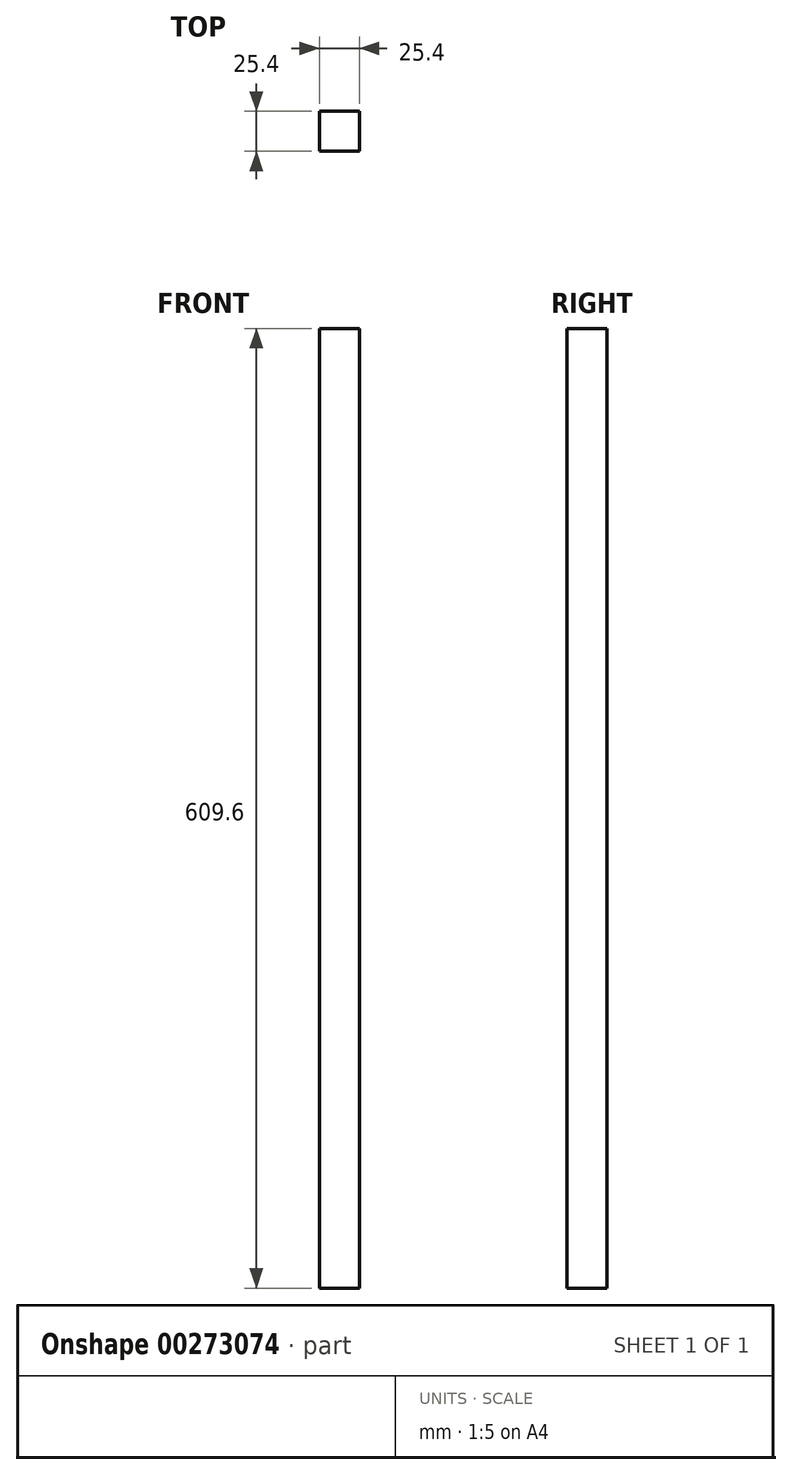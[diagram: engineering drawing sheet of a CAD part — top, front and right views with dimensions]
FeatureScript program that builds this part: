
annotation { "Feature Type Name" : "Feature", "Feature Type Description" : "" }
export const myFeature = defineFeature(function(context is Context, id is Id, definition is map)
    precondition{}
    {
        {
            var Q0;
            Q0=qCreatedBy(makeId("Front.planeOp"),FACE);
            var sketch = newSketch(context, id + "F0", { "sketchPlane" : qUnion([Q0])});
            skLineSegment(sketch, "E0.bottom", {"start": v(-9.09, 529) * mm, "end": v(16.31, 529) * mm});
            skLineSegment(sketch, "E0.top", {"start": v(-9.09, -80.6) * mm, "end": v(16.31, -80.6) * mm});
            skLineSegment(sketch, "E0.left", {"start": v(-9.09, 529) * mm, "end": v(-9.09, -80.6) * mm});
            skLineSegment(sketch, "E0.right", {"start": v(16.31, 529) * mm, "end": v(16.31, -80.6) * mm});
            skSolve(sketch);
        }
        {
            var Q0;
            Q0 = qSketchRegion(id + "F0", true);
            extrude(context, id + "F1", {"entities" : qUnion([Q0]), "depth" : 25.4 * mm});
        }
    });
